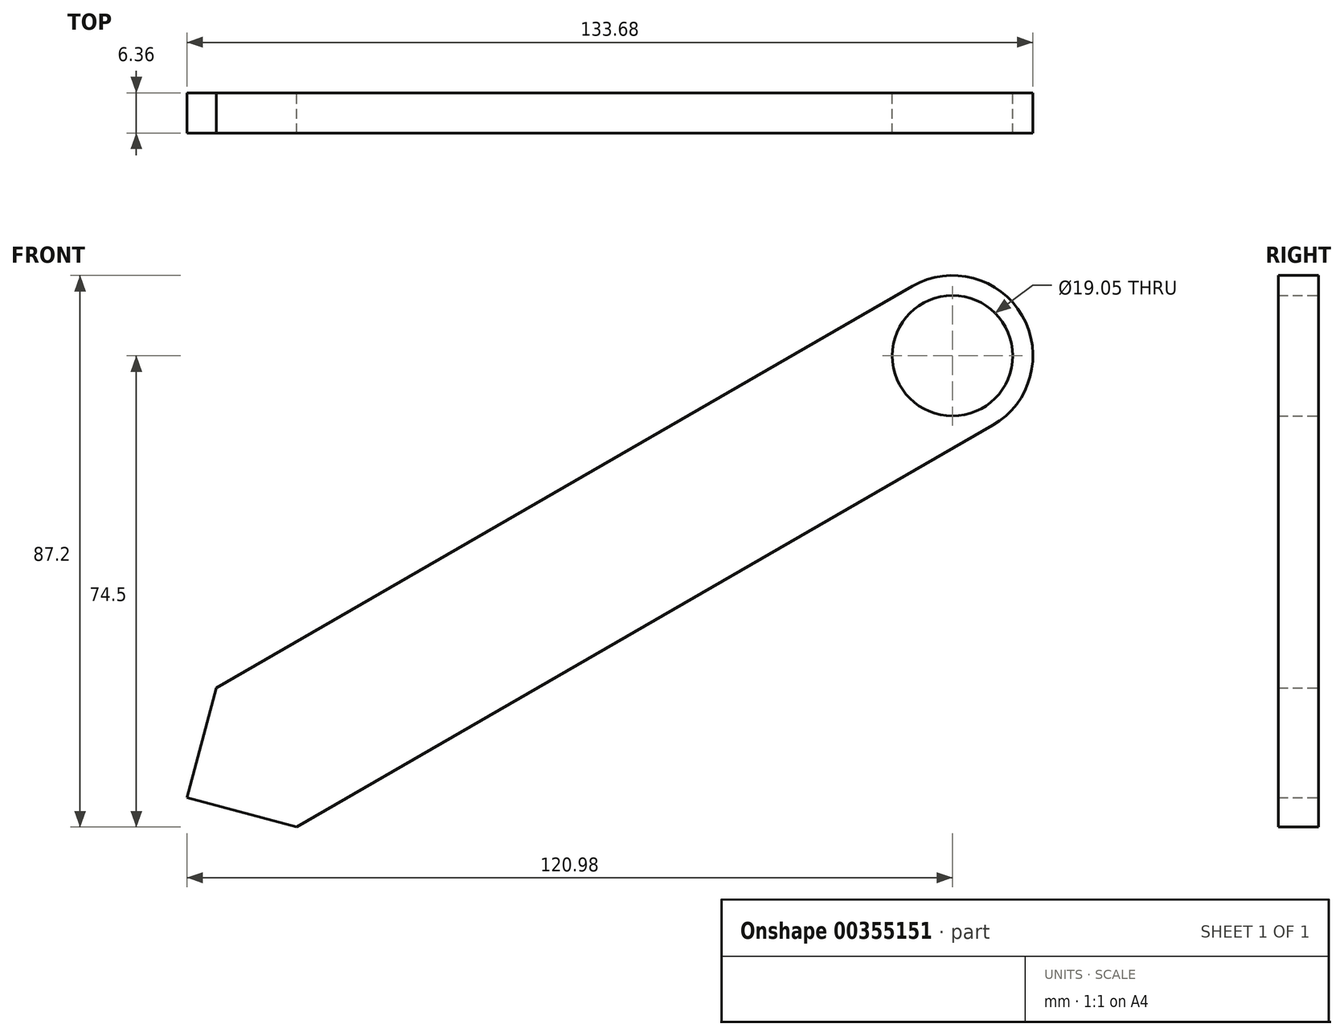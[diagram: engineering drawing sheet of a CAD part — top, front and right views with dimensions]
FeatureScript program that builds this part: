
annotation { "Feature Type Name" : "Feature", "Feature Type Description" : "" }
export const myFeature = defineFeature(function(context is Context, id is Id, definition is map)
    precondition{}
    {
        {
            var Q0;
            Q0=qCreatedBy(makeId("Front.planeOp"),FACE);
            var sketch = newSketch(context, id + "F0", { "sketchPlane" : qUnion([Q0])});
            skLineSegment(sketch, "E0", {"start": v(87.99, -152.4) * mm, "end": v(-263.96, -152.4) * mm});
            skLineSegment(sketch, "E1", {"start": v(-263.96, -152.4) * mm, "end": v(0, 0) * mm});
            skLineSegment(sketch, "E2", {"start": v(0, 0) * mm, "end": v(87.99, -152.4) * mm});
            skLineSegment(sketch, "E3", {"start": v(0, 0) * mm, "end": v(152.4, 87.99) * mm, "construction": true});
            skLineSegment(sketch, "E4", {"start": v(152.4, 87.99) * mm, "end": v(87.99, -152.4) * mm, "construction": true});
            skCircle(sketch, "E5", {"center": v(0, 0) * mm, "radius": 9.53 * mm});
            skCircle(sketch, "E6", {"center": v(0, 0) * mm, "radius": 12.7 * mm});
            skCircle(sketch, "E7", {"center": v(-263.96, -152.4) * mm, "radius": 12.7 * mm});
            skCircle(sketch, "E8", {"center": v(87.99, -152.4) * mm, "radius": 12.7 * mm});
            skLineSegment(sketch, "E9", {"start": v(-6.35, 11) * mm, "end": v(-270.31, -141.4) * mm});
            skLineSegment(sketch, "E10", {"start": v(-263.96, -165.1) * mm, "end": v(87.99, -165.1) * mm});
            skLineSegment(sketch, "E11", {"start": v(98.99, -146.05) * mm, "end": v(11, 6.35) * mm});
            skLineSegment(sketch, "E12", {"start": v(76.99, -158.75) * mm, "end": v(-11, -6.35) * mm});
            skLineSegment(sketch, "E13", {"start": v(-257.61, -163.4) * mm, "end": v(6.35, -11) * mm});
            skLineSegment(sketch, "E14", {"start": v(87.99, -139.7) * mm, "end": v(-263.96, -139.7) * mm});
            skLineSegment(sketch, "E15", {"start": v(87.99, -165.1) * mm, "end": v(109.99, -165.1) * mm});
            skLineSegment(sketch, "E16", {"start": v(98.99, -146.05) * mm, "end": v(109.99, -165.1) * mm});
            skCircle(sketch, "E17", {"center": v(87.99, -152.4) * mm, "radius": 1.59 * mm});
            skCircle(sketch, "E18", {"center": v(-263.96, -152.4) * mm, "radius": 1.59 * mm});
            skLineSegment(sketch, "E19", {"start": v(-270.31, -141.4) * mm, "end": v(-311.36, -165.1) * mm});
            skLineSegment(sketch, "E20", {"start": v(-263.96, -165.1) * mm, "end": v(-311.36, -165.1) * mm});
            skLineSegment(sketch, "E21", {"start": v(-116.34, -52.5) * mm, "end": v(-103.64, -74.5) * mm});
            skLineSegment(sketch, "E22", {"start": v(-116.34, -52.5) * mm, "end": v(-120.98, -69.85) * mm});
            skLineSegment(sketch, "E23", {"start": v(-120.98, -69.85) * mm, "end": v(-103.64, -74.5) * mm});
            skLineSegment(sketch, "E24", {"start": v(-204.32, -103.3) * mm, "end": v(-191.62, -125.3) * mm});
            skLineSegment(sketch, "E25", {"start": v(-191.62, -125.3) * mm, "end": v(-208.97, -120.65) * mm});
            skLineSegment(sketch, "E26", {"start": v(-208.97, -120.65) * mm, "end": v(-204.32, -103.3) * mm});
            skSolve(sketch);
        }
        {
            var Q0;
            {var subQ1=sQuery(id+"F0.wireOp",EDGE,"E1");var subQ3=sQuery(id+"F0.wireOp",EDGE,"E21");var subQ4=makeQuery(id+"F0.imprint","INTERSECT",VERTEX,{"derivedFrom":[subQ1,subQ3]});Q0=makeQuery(id+"F0.imprint","IMPRINT",FACE,{"disambiguationData":[TD([[makeQuery(id+"F0.imprint","IMPRINT",EDGE,{"disambiguationData":[TD([[subQ4,-1.0]])],"derivedFrom":subQ1}),1.0]])]});}
            var Q1;
            {var subQ0=sQuery(id+"F0.wireOp",EDGE,"E5");var subQ1=sQuery(id+"F0.wireOp",EDGE,"E1");var subQ2=makeQuery(id+"F0.imprint","INTERSECT",VERTEX,{"derivedFrom":[subQ1,subQ0]});Q1=makeQuery(id+"F0.imprint","IMPRINT",FACE,{"disambiguationData":[TD([[makeQuery(id+"F0.imprint","IMPRINT",EDGE,{"disambiguationData":[TD([[subQ2,1.0]])],"derivedFrom":subQ0}),-1.0]])]});}
            var Q2;
            {var subQ1=sQuery(id+"F0.wireOp",EDGE,"E1");var subQ3=sQuery(id+"F0.wireOp",EDGE,"E5");var subQ4=makeQuery(id+"F0.imprint","INTERSECT",VERTEX,{"derivedFrom":[subQ1,subQ3]});Q2=makeQuery(id+"F0.imprint","IMPRINT",FACE,{"disambiguationData":[TD([[makeQuery(id+"F0.imprint","IMPRINT",EDGE,{"disambiguationData":[TD([[subQ4,-1.0]])],"derivedFrom":subQ3}),-1.0]])]});}
            var Q3;
            {var subQ0=sQuery(id+"F0.wireOp",EDGE,"E12");var subQ3=sQuery(id+"F0.wireOp",EDGE,"E13");var subQ5=makeQuery(id+"F0.imprint","INTERSECT",VERTEX,{"derivedFrom":[subQ0,subQ3]});Q3=makeQuery(id+"F0.imprint","IMPRINT",FACE,{"disambiguationData":[TD([[makeQuery(id+"F0.imprint","IMPRINT",EDGE,{"disambiguationData":[TD([[subQ5,-1.0]])],"derivedFrom":subQ0}),-1.0]])]});}
            var Q4;
            {var subQ1=sQuery(id+"F0.wireOp",EDGE,"E1");var subQ3=sQuery(id+"F0.wireOp",EDGE,"E21");var subQ4=makeQuery(id+"F0.imprint","INTERSECT",VERTEX,{"derivedFrom":[subQ1,subQ3]});Q4=makeQuery(id+"F0.imprint","IMPRINT",FACE,{"disambiguationData":[TD([[makeQuery(id+"F0.imprint","IMPRINT",EDGE,{"disambiguationData":[TD([[subQ4,-1.0]])],"derivedFrom":subQ1}),-1.0]])]});}
            var Q5;
            {var subQ0=sQuery(id+"F0.wireOp",EDGE,"E22");Q5=makeQuery(id+"F0.imprint","IMPRINT",FACE,{"disambiguationData":[TD([[makeQuery(id+"F0.imprint","IMPRINT",EDGE,{"derivedFrom":subQ0}),1.0]])]});}
            var Q6;
            {var subQ0=sQuery(id+"F0.wireOp",EDGE,"E23");Q6=makeQuery(id+"F0.imprint","IMPRINT",FACE,{"disambiguationData":[TD([[makeQuery(id+"F0.imprint","IMPRINT",EDGE,{"derivedFrom":subQ0}),1.0]])]});}
            extrude(context, id + "F1", {"entities" : qUnion([Q0, Q1, Q2, Q3, Q4, Q5, Q6]), "endBound" : BoundingType.SYMMETRIC, "depth" : 6.35 * mm});
        }
    });
